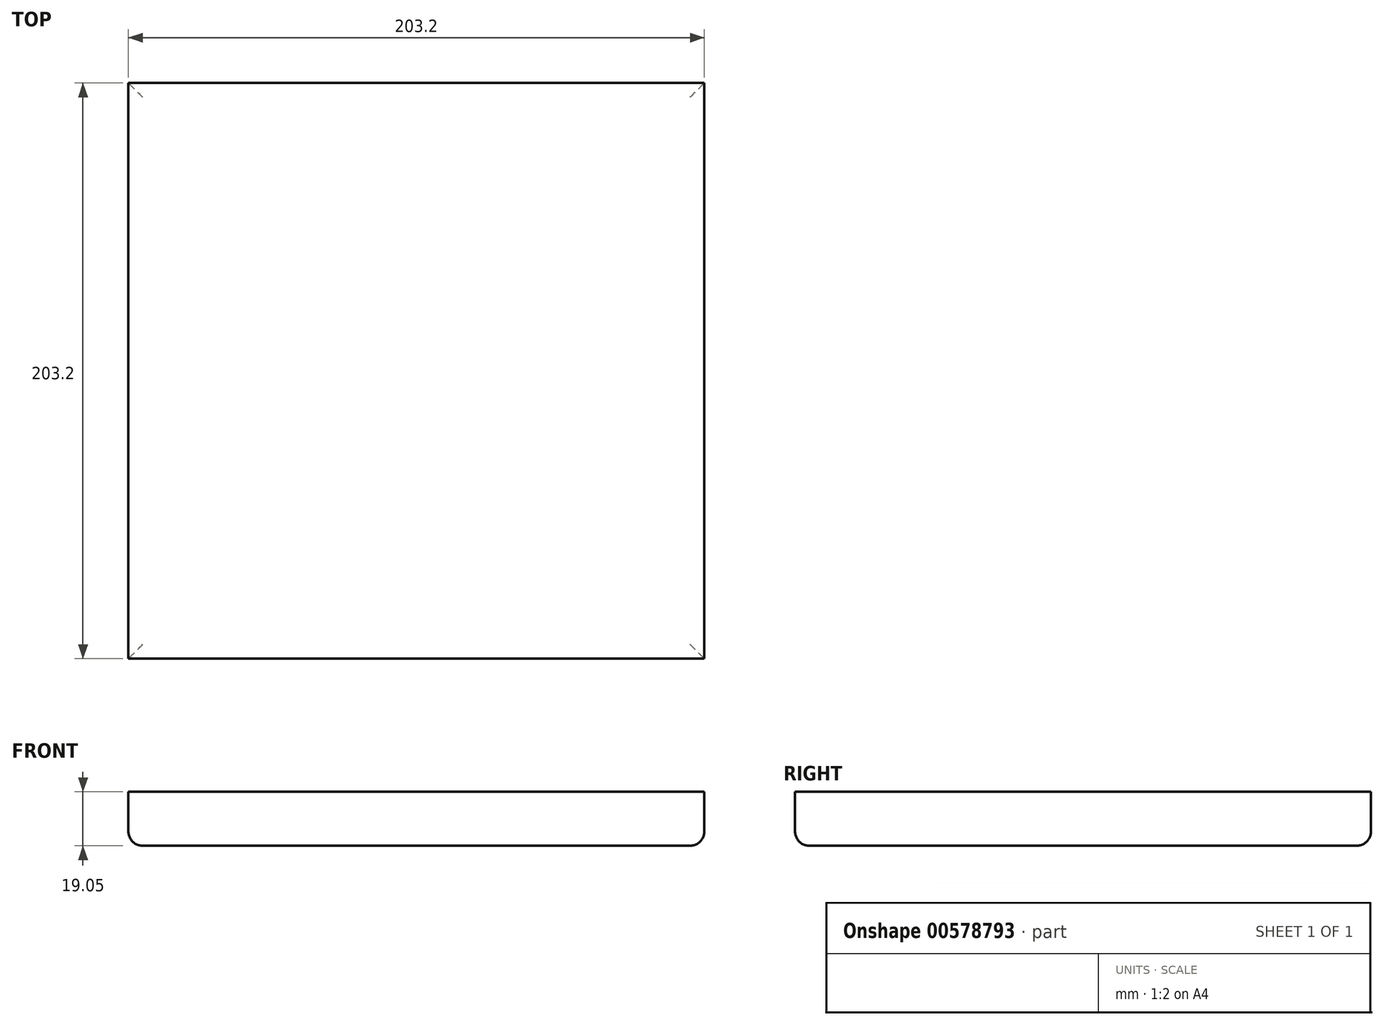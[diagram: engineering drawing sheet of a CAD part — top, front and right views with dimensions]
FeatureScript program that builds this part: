
annotation { "Feature Type Name" : "Feature", "Feature Type Description" : "" }
export const myFeature = defineFeature(function(context is Context, id is Id, definition is map)
    precondition{}
    {
        {
            var Q0;
            Q0=qCreatedBy(makeId("Top.planeOp"),FACE);
            var sketch = newSketch(context, id + "F0", { "sketchPlane" : qUnion([Q0])});
            skLineSegment(sketch, "E0.bottom", {"start": v(-64.03, 150.54) * mm, "end": v(139.17, 150.54) * mm});
            skLineSegment(sketch, "E0.top", {"start": v(-64.03, -52.66) * mm, "end": v(139.17, -52.66) * mm});
            skLineSegment(sketch, "E0.left", {"start": v(-64.03, 150.54) * mm, "end": v(-64.03, -52.66) * mm});
            skLineSegment(sketch, "E0.right", {"start": v(139.17, 150.54) * mm, "end": v(139.17, -52.66) * mm});
            skSolve(sketch);
        }
        {
            var Q0;
            Q0=makeQuery(id+"F0.imprint","IMPRINT",FACE,{"disambiguationData":[TD([[makeQuery(id+"F0.imprint","IMPRINT",EDGE,{"derivedFrom":sQuery(id+"F0.wireOp",EDGE,"E0.bottom")}),-1.0]])]});
            extrude(context, id + "F1", {"entities" : qUnion([Q0]), "depth" : 19.05 * mm, "offsetDistance" : 25.4 * mm});
        }
        {
            var Q0;
            Q0=makeQuery(id+"F1.opExtrude","CAP_FACE",FACE,{"disambiguationData":[OSD([sQuery(id+"F0.wireOp",EDGE,"E0.bottom"),sQuery(id+"F0.wireOp",EDGE,"E0.top"),sQuery(id+"F0.wireOp",EDGE,"E0.left"),sQuery(id+"F0.wireOp",EDGE,"E0.right")])],"isStart":true});
            fillet(context, id + "F2", {"entities" : qUnion([Q0]), "radius" : 5.08 * mm, "tangentPropagation" : true, "allowEdgeOverflow" : false});
        }
    });
